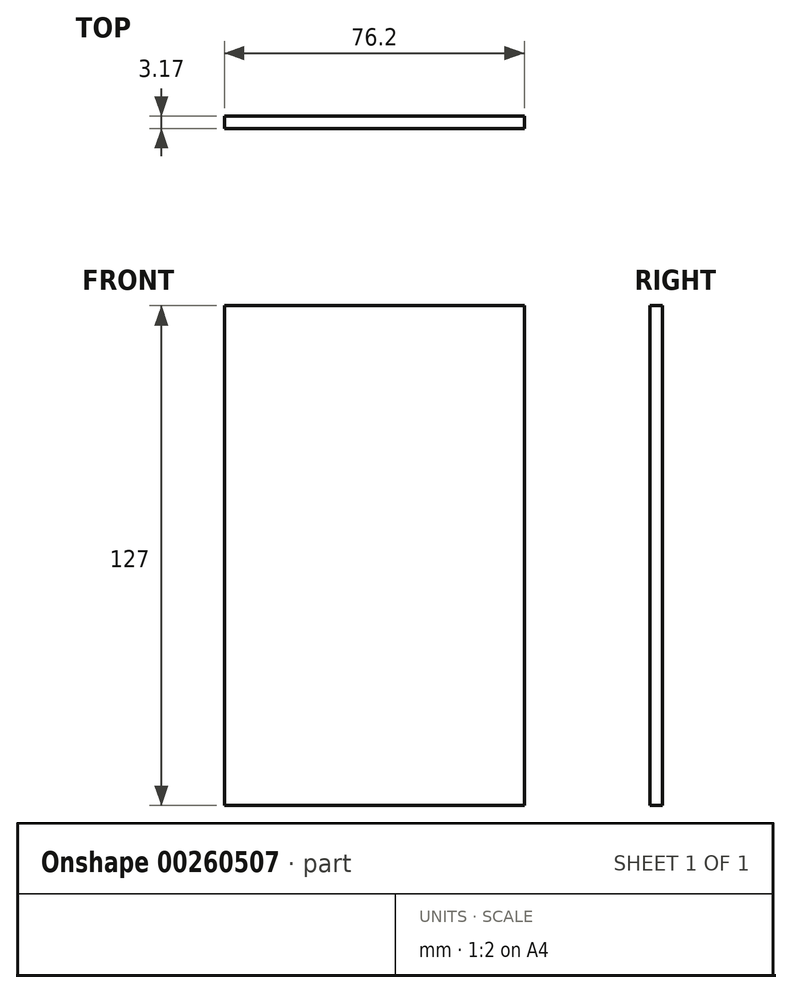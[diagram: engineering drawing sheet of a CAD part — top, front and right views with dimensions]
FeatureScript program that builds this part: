
annotation { "Feature Type Name" : "Feature", "Feature Type Description" : "" }
export const myFeature = defineFeature(function(context is Context, id is Id, definition is map)
    precondition{}
    {
        {
            var Q0;
            Q0=qCreatedBy(makeId("Front.planeOp"),FACE);
            var sketch = newSketch(context, id + "F0", { "sketchPlane" : qUnion([Q0])});
            skLineSegment(sketch, "E0.bottom", {"start": v(-38.1, -63.5) * mm, "end": v(38.1, -63.5) * mm});
            skLineSegment(sketch, "E0.top", {"start": v(-38.1, 63.5) * mm, "end": v(38.1, 63.5) * mm});
            skLineSegment(sketch, "E0.left", {"start": v(-38.1, -63.5) * mm, "end": v(-38.1, 63.5) * mm});
            skLineSegment(sketch, "E0.right", {"start": v(38.1, -63.5) * mm, "end": v(38.1, 63.5) * mm});
            skPoint(sketch, "E0.middle", {"position": v(0, 0) * mm});
            skSolve(sketch);
        }
        {
            var Q0;
            Q0 = qSketchRegion(id + "F0", true);
            extrude(context, id + "F1", {"entities" : qUnion([Q0]), "depth" : 3.17 * mm});
        }
    });
